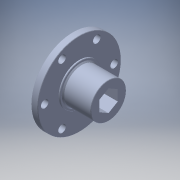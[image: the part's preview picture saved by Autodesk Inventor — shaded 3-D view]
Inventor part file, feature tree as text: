
AUTODESK INVENTOR PART (.ipt)
format: ipt  version: 2016 (Build 200138000, 138)  size: 169,472 bytes
history: native  units: in
note: dims shown in document units (in); Inventor stores cm internally (conversion verified against a paired STEP export)
features: chamfer x1
ambient origin geometry x8: Origin, YZ Plane, XZ Plane, XY Plane, X Axis, Y Axis, Z Axis, Center Point
bodies: Solid1 (feature_tree)
feature tree (1):
  chamfer  "Chamfer3"  [1 undecoded]
note: 1 required parameter value undecoded (feature->parameter linkage not recoverable at this tier; creation-order binding heuristic only, values carry confidence <= 0.55)
